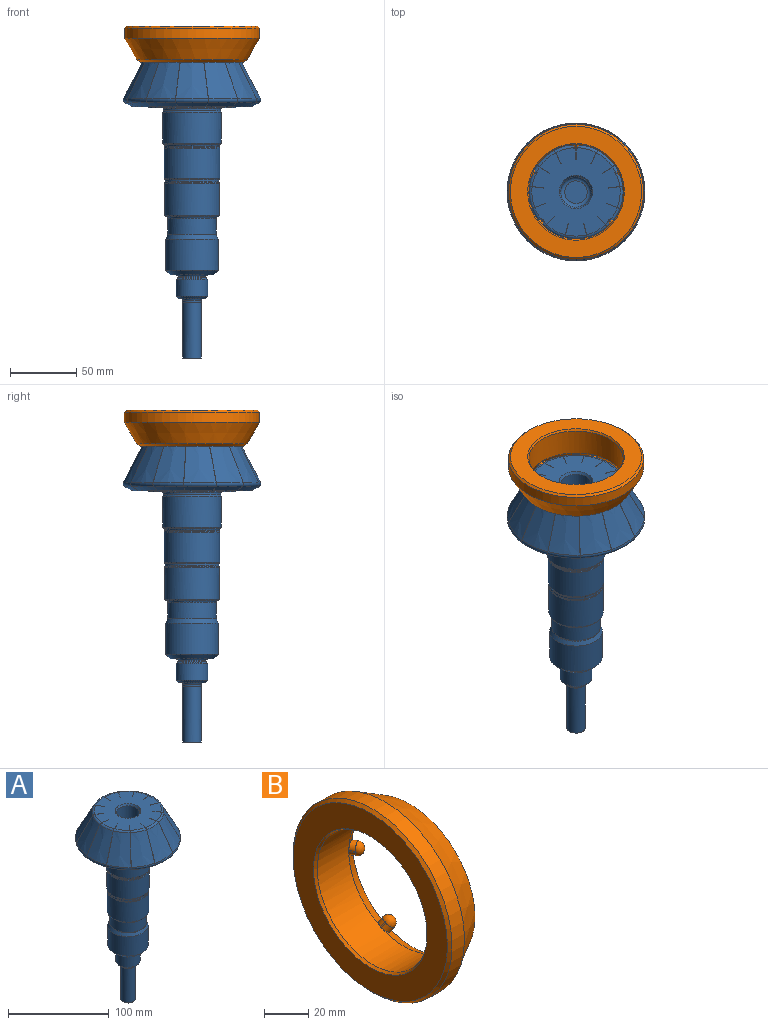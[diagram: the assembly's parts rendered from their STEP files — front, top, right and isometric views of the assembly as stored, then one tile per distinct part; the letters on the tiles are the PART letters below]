
ASSEMBLY  parts=2 mates=1
PART A: 145 faces, bbox 111.8x111x228.1 mm
  f0: cone r=0mm half-angle=45deg, axis (0,0,-1), area 6.9mm2, adj f1
  f1: cylinder r=1.25mm len=2.5mm, axis (0,0,-1), area 7.3mm2, adj f0,f2
  f2: cone r=0mm half-angle=30deg, axis (0,0,-1), area 34.3mm2, adj f1,f3
  f3: cone r=0mm half-angle=60deg, axis (0,0,-1), area 33.6mm2, adj f2,f4
  f4: plane 14x14mm, normal (0,0,-1), area 102.8mm2, adj f3,f5
  f5: cylinder r=7mm len=41.51mm, axis (0,0,1), area 1825.8mm2, adj f4,f6
  f6: cone r=0mm half-angle=20deg, axis (0,0,-1), area 6.4mm2, adj f5,f7
  f7: cylinder r=6.95mm len=13.9mm, axis (0,0,1), area 87.3mm2, adj f6,f8
  f8: torus R=7.95mm, axis (0,0,1), area 72.2mm2, adj f7,f9
  f9: plane 20x20mm, normal (0,0,-1), area 115.6mm2, adj f8,f10
  f10: cone r=0mm half-angle=45deg, axis (0,0,1), area 195.5mm2, adj f9,f11
  f11: cylinder r=12mm len=24mm, axis (0,0,1), area 953.1mm2, adj f10,f12
  f12: cone r=0mm half-angle=50deg, axis (0,0,-1), area 100.7mm2, adj f11,f13
  f13: torus R=11.7mm, axis (0,0,1), area 70.1mm2, adj f12,f14
  f14: cylinder r=10.5mm len=21mm, axis (0,0,1), area 22.5mm2, adj f13,f15
  f15: torus R=11.7mm, axis (0,0,1), area 129.5mm2, adj f14,f16
  f16: plane 33x33mm, normal (0,0,-1), area 425.2mm2, adj f15,f17
  f17: cone r=0mm half-angle=45deg, axis (0,0,1), area 545.4mm2, adj f16,f18
  f18: cylinder r=19.88mm len=39.75mm, axis (0,0,1), area 2938.8mm2, adj f17,f19
  f19: cone r=0mm half-angle=25deg, axis (0,0,-1), area 443.6mm2, adj f18,f20
  f20: torus R=19.4mm, axis (0,0,1), area 60mm2, adj f19,f21
  f21: cylinder r=18.2mm len=36.4mm, axis (0,0,1), area 1376.1mm2, adj f20,f22
  f22: torus R=19.4mm, axis (0,0,1), area 220.7mm2, adj f21,f23
  f23: plane 40.12x40.12mm, normal (0,0,-1), area 81.8mm2, adj f22,f24
  f24: cone r=0mm half-angle=30deg, axis (0,0,1), area 147.6mm2, adj f23,f25
  f25: cylinder r=20.64mm len=41.28mm, axis (0,0,1), area 3145.3mm2, adj f24,f26
  f26: cone r=0mm half-angle=25deg, axis (0,0,-1), area 57.3mm2, adj f25,f27
  f27: torus R=21.54mm, axis (0,0,1), area 67mm2, adj f26,f28
  f28: cylinder r=20.34mm len=40.68mm, axis (0,0,1), area 193.3mm2, adj f27,f29
  f29: torus R=21.54mm, axis (0,0,1), area 80.5mm2, adj f28,f30
  f30: cone r=0mm half-angle=30deg, axis (0,0,1), area 130.8mm2, adj f29,f31
  f31: cylinder r=21mm len=42mm, axis (0,0,1), area 2983.2mm2, adj f30,f32
  f32: cone r=0mm half-angle=25deg, axis (0,0,-1), area 58.3mm2, adj f31,f33
  f33: torus R=21.9mm, axis (0,0,1), area 68.2mm2, adj f32,f34
  f34: cylinder r=20.7mm len=41.4mm, axis (0,0,1), area 82.5mm2, adj f33,f35
  f35: torus R=21.9mm, axis (0,0,1), area 113.4mm2, adj f34,f36
  f36: cylinder r=21mm len=42mm, axis (0,0,1), area 53.6mm2, adj f35,f37
  f37: plane 43.3x43.3mm, normal (0,0,-1), area 86.8mm2, adj f36,f38
  f38: cone r=0mm half-angle=30deg, axis (0,0,1), area 159.2mm2, adj f37,f39
  f39: cylinder r=22.23mm len=44.45mm, axis (0,0,1), area 3259.8mm2, adj f38,f40
  f40: cone r=0mm half-angle=25deg, axis (0,0,-1), area 159.3mm2, adj f39,f41
  f41: torus R=22.46mm, axis (0,0,1), area 47.6mm2, adj f40,f42
  f42: cylinder r=21.66mm len=43.33mm, axis (0,0,1), area 152.8mm2, adj f41,f43
  f43: torus R=22.46mm, axis (0,0,1), area 173.3mm2, adj f42,f45
  f44: plane 17.03x17.01mm, normal (0,0,1), area 227mm2, adj f46
  f45: plane 53.33x53.33mm, normal (0,0,-1), area 648.2mm2, adj f43,f47
  f46: torus R=8.5mm, axis (0,0,-1), area 308.2mm2, adj f44,f48
  f47: cylinder r=26.66mm len=53.33mm, axis (0,0,1), area 25.1mm2, adj f45,f73
  f48: cylinder r=11.5mm len=100mm, axis (0,0,-1), area 7225.7mm2, adj f46,f86
  f49: torus R=49.52mm, axis (0,0,-1), area 97.6mm2, adj f50,f89,f90,f91
  f50: cone r=0mm half-angle=27.8deg, axis (0,0,-1), area 728.3mm2, adj f49,f75,f89,f91
  f51: torus R=49.52mm, axis (0,0,-1), area 97.6mm2, adj f52,f93,f94,f95
  f52: cone r=0mm half-angle=27.8deg, axis (0,0,-1), area 728.3mm2, adj f51,f76,f93,f95
  f53: torus R=49.52mm, axis (0,0,-1), area 97.6mm2, adj f54,f97,f98,f99
  f54: cone r=0mm half-angle=27.8deg, axis (0,0,-1), area 728.3mm2, adj f53,f77,f97,f99
  f55: torus R=49.52mm, axis (0,0,-1), area 97.6mm2, adj f56,f101,f102,f103
  f56: cone r=0mm half-angle=27.8deg, axis (0,0,-1), area 728.3mm2, adj f55,f78,f101,f103
  f57: torus R=49.52mm, axis (0,0,-1), area 97.6mm2, adj f58,f105,f106,f107
  f58: cone r=0mm half-angle=27.8deg, axis (0,0,-1), area 728.3mm2, adj f57,f79,f105,f107
  f59: torus R=49.52mm, axis (0,0,-1), area 97.6mm2, adj f60,f109,f110,f111
  f60: cone r=0mm half-angle=27.8deg, axis (0,0,-1), area 728.3mm2, adj f59,f80,f109,f111
  f61: torus R=49.52mm, axis (0,0,-1), area 97.6mm2, adj f62,f113,f114,f115
  f62: cone r=0mm half-angle=27.8deg, axis (0,0,-1), area 728.3mm2, adj f61,f81,f113,f115
  f63: torus R=49.52mm, axis (0,0,-1), area 97.6mm2, adj f64,f117,f118,f119
  f64: cone r=0mm half-angle=27.8deg, axis (0,0,-1), area 728.3mm2, adj f63,f82,f117,f119
  f65: torus R=49.52mm, axis (0,0,-1), area 97.6mm2, adj f66,f121,f122,f123
  f66: cone r=0mm half-angle=27.8deg, axis (0,0,-1), area 728.3mm2, adj f65,f83,f121,f123
  f67: torus R=49.52mm, axis (0,0,-1), area 97.6mm2, adj f68,f125,f126,f127
  f68: cone r=0mm half-angle=27.8deg, axis (0,0,-1), area 728.3mm2, adj f67,f84,f125,f127
  f69: torus R=49.52mm, axis (0,0,-1), area 97.6mm2, adj f70,f129,f130,f131
  f70: cone r=0mm half-angle=27.8deg, axis (0,0,-1), area 728.3mm2, adj f69,f85,f129,f131
  f71: torus R=49.52mm, axis (0,0,-1), area 97.6mm2, adj f72,f87,f88,f133
  f72: cone r=0mm half-angle=27.8deg, axis (0,0,-1), area 728.3mm2, adj f71,f74,f88,f133
  f73: plane 66x66mm, normal (0,0,-1), area 1187.9mm2, adj f47,f134
  f74: torus R=33.34mm, axis (0,0,-1), area 45.1mm2, adj f72,f88,f133,f138
  f75: torus R=33.34mm, axis (0,0,-1), area 45.1mm2, adj f50,f89,f91,f138
  f76: torus R=33.34mm, axis (0,0,-1), area 45.1mm2, adj f52,f93,f95,f138
  f77: torus R=33.34mm, axis (0,0,-1), area 45.1mm2, adj f54,f97,f99,f138
  f78: torus R=33.34mm, axis (0,0,-1), area 45.1mm2, adj f56,f101,f103,f138
  f79: torus R=33.34mm, axis (0,0,-1), area 45.1mm2, adj f58,f105,f107,f138
  f80: torus R=33.34mm, axis (0,0,-1), area 45.1mm2, adj f60,f109,f111,f138
  f81: torus R=33.34mm, axis (0,0,-1), area 45.1mm2, adj f62,f113,f115,f138
  f82: torus R=33.34mm, axis (0,0,-1), area 45.1mm2, adj f64,f117,f119,f138
  f83: torus R=33.34mm, axis (0,0,-1), area 45.1mm2, adj f66,f121,f123,f138
  f84: torus R=33.34mm, axis (0,0,-1), area 45.1mm2, adj f68,f125,f127,f138
  f85: torus R=33.34mm, axis (0,0,-1), area 45.1mm2, adj f70,f129,f131,f138
  f86: cone r=0mm half-angle=30deg, axis (0,0,1), area 175.2mm2, adj f48,f138
  f87: cone r=0mm half-angle=62.2deg, axis (0,0,1), area 147.6mm2, adj f71,f88,f133,f140
  f88: plane 38.41x27.58mm, normal (1,0,0), area 377.1mm2, adj f71,f72,f74,f87,f135,f138,f140
  f89: plane 38.41x24.42mm, normal (-0.89,0.46,0), area 377.1mm2, adj f49,f50,f75,f90,f138,f139,f140
  f90: cone r=0mm half-angle=62.2deg, axis (0,0,1), area 147.6mm2, adj f49,f89,f91,f140
  f91: plane 38.41x22.7mm, normal (0.57,-0.82,0), area 377.1mm2, adj f49,f50,f75,f90,f92,f138,f140
  f92: plane 38.4x16.7mm, normal (0.73,0.5,0.47), area 4.3mm2, adj f91,f93,f138,f140
  f93: plane 38.41x22.7mm, normal (-0.57,0.82,0), area 377.1mm2, adj f51,f52,f76,f92,f94,f138,f140
  f94: cone r=0mm half-angle=62.2deg, axis (0,0,1), area 147.6mm2, adj f51,f93,f95,f140
  f95: plane 38.41x27.38mm, normal (0.12,-0.99,0), area 377.1mm2, adj f51,f52,f76,f94,f96,f138,f140
  f96: plane 38.4x20.09mm, normal (0.88,0.11,0.47), area 4.3mm2, adj f95,f97,f138,f140
  f97: plane 38.41x27.38mm, normal (-0.12,0.99,0), area 377.1mm2, adj f53,f54,f77,f96,f98,f138,f140
  f98: cone r=0mm half-angle=62.2deg, axis (0,0,1), area 147.6mm2, adj f53,f97,f99,f140
  f99: plane 38.41x25.79mm, normal (-0.35,-0.94,0), area 377.1mm2, adj f53,f54,f77,f98,f100,f138,f140
  f100: plane 38.4x18.95mm, normal (0.83,-0.31,0.47), area 4.3mm2, adj f99,f101,f138,f140
  f101: plane 38.41x25.79mm, normal (0.35,0.94,0), area 377.1mm2, adj f55,f56,f78,f100,f102,f138,f140
  f102: cone r=0mm half-angle=62.2deg, axis (0,0,1), area 147.6mm2, adj f55,f101,f103,f140
  f103: plane 38.41x20.64mm, normal (-0.75,-0.66,0), area 377.1mm2, adj f55,f56,f78,f102,f104,f138,f140
  f104: plane 38.4x15.21mm, normal (0.59,-0.66,0.47), area 4.3mm2, adj f103,f105,f138,f140
  f105: plane 38.41x20.65mm, normal (0.75,0.66,0), area 377.1mm2, adj f57,f58,f79,f104,f106,f138,f140
  f106: cone r=0mm half-angle=62.2deg, axis (0,0,1), area 147.6mm2, adj f57,f105,f107,f140
  f107: plane 38.41x26.78mm, normal (-0.97,-0.24,0), area 377.1mm2, adj f57,f58,f79,f106,f108,f138,f140
  f108: plane 38.4x19.66mm, normal (0.21,-0.86,0.47), area 4.3mm2, adj f107,f109,f138,f140
  f109: plane 38.41x26.78mm, normal (0.97,0.24,0), area 377.1mm2, adj f59,f60,f80,f108,f110,f138,f140
  f110: cone r=0mm half-angle=62.2deg, axis (0,0,1), area 147.6mm2, adj f59,f109,f111,f140
  f111: plane 38.41x26.78mm, normal (-0.97,0.24,0), area 377.1mm2, adj f59,f60,f80,f110,f112,f138,f140
  f112: plane 38.4x19.66mm, normal (-0.21,-0.86,0.47), area 4.3mm2, adj f111,f113,f138,f140
  f113: plane 38.41x26.78mm, normal (0.97,-0.24,0), area 377.1mm2, adj f61,f62,f81,f112,f114,f138,f140
  f114: cone r=0mm half-angle=62.2deg, axis (0,0,1), area 147.6mm2, adj f61,f113,f115,f140
  f115: plane 38.41x20.64mm, normal (-0.75,0.66,0), area 377.1mm2, adj f61,f62,f81,f114,f116,f138,f140
  f116: plane 38.4x15.21mm, normal (-0.59,-0.66,0.47), area 4.3mm2, adj f115,f117,f138,f140
  f117: plane 38.41x20.65mm, normal (0.75,-0.66,0), area 377.1mm2, adj f63,f64,f82,f116,f118,f138,f140
  f118: cone r=0mm half-angle=62.2deg, axis (0,0,1), area 147.6mm2, adj f63,f117,f119,f140
  f119: plane 38.41x25.79mm, normal (-0.35,0.94,0), area 377.1mm2, adj f63,f64,f82,f118,f120,f138,f140
  f120: plane 38.4x18.95mm, normal (-0.83,-0.31,0.47), area 4.3mm2, adj f119,f121,f138,f140
  f121: plane 38.41x25.79mm, normal (0.35,-0.94,0), area 377.1mm2, adj f65,f66,f83,f120,f122,f138,f140
  f122: cone r=0mm half-angle=62.2deg, axis (0,0,1), area 147.6mm2, adj f65,f121,f123,f140
  f123: plane 38.41x27.38mm, normal (0.12,0.99,0), area 377.1mm2, adj f65,f66,f83,f122,f124,f138,f140
  f124: plane 38.4x20.09mm, normal (-0.88,0.11,0.47), area 4.3mm2, adj f123,f125,f138,f140
  f125: plane 38.41x27.38mm, normal (-0.12,-0.99,0), area 377.1mm2, adj f67,f68,f84,f124,f126,f138,f140
  f126: cone r=0mm half-angle=62.2deg, axis (0,0,1), area 147.6mm2, adj f67,f125,f127,f140
  f127: plane 38.41x22.7mm, normal (0.57,0.82,0), area 377.1mm2, adj f67,f68,f84,f126,f128,f138,f140
  f128: plane 38.4x16.7mm, normal (-0.73,0.5,0.47), area 4.3mm2, adj f127,f129,f138,f140
  f129: plane 38.41x22.7mm, normal (-0.57,-0.82,0), area 377.1mm2, adj f69,f70,f85,f128,f130,f138,f140
  f130: cone r=0mm half-angle=62.2deg, axis (0,0,1), area 147.6mm2, adj f69,f129,f131,f140
  f131: plane 38.41x24.42mm, normal (0.89,0.46,0), area 377.1mm2, adj f69,f70,f85,f130,f132,f138,f140
  f132: plane 38.4x17.96mm, normal (-0.41,0.78,0.47), area 4.3mm2, adj f131,f133,f138,f140
  f133: plane 38.41x24.42mm, normal (-0.89,-0.46,0), area 377.1mm2, adj f71,f72,f74,f87,f132,f138,f140
  f134: cylinder r=33mm len=66mm, axis (0,0,-1), area 207.3mm2, adj f73,f140
  f135: plane 38.4x20.23mm, normal (0,0.88,0.47), area 4.3mm2, adj f88,f138,f140,f141
  f136: cone r=0mm half-angle=27.8deg, axis (0,0,-1), area 728.3mm2, adj f137,f141,f142,f143
  f137: torus R=33.34mm, axis (0,0,-1), area 45.1mm2, adj f136,f138,f141,f143
  f138: plane 66.69x66.69mm, normal (0,0,1), area 2978.4mm2, adj f74,f75,f76,f77,f78,f79,f80,f81
  f139: plane 38.4x17.96mm, normal (0.41,0.78,0.47), area 4.3mm2, adj f89,f138,f140,f143
  f140: plane 90.02x90.02mm, normal (0,0,-1), area 2942.8mm2, adj f87,f88,f89,f90,f91,f92,f93,f94
  f141: plane 38.4x27.58mm, normal (-1,0,0), area 377.1mm2, adj f135,f136,f137,f138,f140,f142,f144
  f142: torus R=49.52mm, axis (0,0,-1), area 97.6mm2, adj f136,f141,f143,f144
  f143: plane 38.41x24.42mm, normal (0.89,-0.46,0), area 377.1mm2, adj f136,f137,f138,f139,f140,f142,f144
  f144: cone r=0mm half-angle=62.2deg, axis (0,0,1), area 147.6mm2, adj f140,f141,f142,f143
PART B: 37 faces, bbox 30.8x103.3x103.3 mm
  f0: plane 4.35x3.07mm, normal (-0.87,-0.5,0), area 2.2mm2, adj f1,f20,f21,f23
  f1: cylinder r=35.56mm len=71.12mm, axis (-1,0,0), area 4512.5mm2, adj f0,f2,f3,f4,f5,f6,f7,f10
  f2: cone r=36mm half-angle=30deg, axis (-1,0,0), area 398mm2, adj f1,f26
  f3: cone r=37.13mm half-angle=30deg, axis (1,0,0), area 232.4mm2, adj f1,f8,f23,f27
  f4: cone r=37.13mm half-angle=30deg, axis (1,0,0), area 228.3mm2, adj f1,f8,f29,f32
  f5: cone r=37.13mm half-angle=30deg, axis (1,0,0), area 366.1mm2, adj f1,f8,f10,f34
  f6: cone r=37.13mm half-angle=30deg, axis (1,0,0), area 228.4mm2, adj f1,f8,f17,f20
  f7: cone r=37.13mm half-angle=30deg, axis (1,0,0), area 228.4mm2, adj f1,f8,f12,f15
  f8: cone r=40.22mm half-angle=60deg, axis (-1,0,0), area 886.8mm2, adj f3,f4,f5,f6,f7,f9,f10,f12
  f9: cone r=46.36mm half-angle=30deg, axis (-1,0,0), area 5381mm2, adj f8,f24
  f10: cylinder r=3.17mm len=7.08mm, axis (-0.5,-0.56,-0.66), area 30.5mm2, adj f1,f5,f8,f11,f13,f14
  f11: plane 3.93x3.66mm, normal (-0.87,0.32,0.38), area 2.2mm2, adj f1,f10,f12,f14
  f12: cylinder r=3.17mm len=7.08mm, axis (0.5,0.56,0.66), area 30.5mm2, adj f1,f7,f8,f11,f13,f14
  f13: plane 3.9x3.63mm, normal (0.87,-0.32,-0.38), area 2.2mm2, adj f8,f10,f12,f14
  f14: torus R=0.33mm, axis (-0.87,0.32,0.38), area 180.8mm2, adj f10,f11,f12,f13
  f15: cylinder r=3.17mm len=7.08mm, axis (-0.5,0.36,-0.79), area 30.5mm2, adj f1,f7,f8,f16,f18,f19
  f16: plane 4.24x3.08mm, normal (-0.87,-0.21,0.45), area 2.2mm2, adj f1,f15,f17,f19
  f17: cylinder r=3.17mm len=7.08mm, axis (0.5,-0.36,0.79), area 30.5mm2, adj f1,f6,f8,f16,f18,f19
  f18: plane 4.21x3.07mm, normal (0.87,0.21,-0.45), area 2.2mm2, adj f8,f15,f17,f19
  f19: torus R=0.33mm, axis (-0.87,-0.21,0.45), area 180.8mm2, adj f15,f16,f17,f18
  f20: cylinder r=3.17mm len=7.08mm, axis (-0.5,0.87,-0.01), area 30.5mm2, adj f0,f1,f6,f8,f21,f22
  f21: torus R=0.33mm, axis (-0.87,-0.5,0), area 180.8mm2, adj f0,f20,f22,f23
  f22: plane 4.32x3.05mm, normal (0.87,0.5,0), area 2.2mm2, adj f8,f20,f21,f23
  f23: cylinder r=3.17mm len=7.08mm, axis (0.5,-0.87,0.01), area 30.5mm2, adj f0,f1,f3,f8,f21,f22
  f24: cylinder r=50.98mm len=101.96mm, axis (-1,0,0), area 2527.8mm2, adj f9,f25
  f25: cone r=50.22mm half-angle=45deg, axis (1,0,0), area 680mm2, adj f24,f26
  f26: plane 98.91x98.91mm, normal (-1,0,0), area 3511.7mm2, adj f2,f25
  f27: cylinder r=3.17mm len=7.08mm, axis (-0.5,0.36,0.79), area 30.5mm2, adj f1,f3,f8,f28,f30,f31
  f28: plane 3.01x1.83mm, normal (-0.87,-0.21,-0.46), area 2.2mm2, adj f1,f27,f29,f31
  f29: cylinder r=3.17mm len=7.08mm, axis (0.5,-0.36,-0.79), area 30.5mm2, adj f1,f4,f8,f28,f30,f31
  f30: plane 2.98x1.82mm, normal (0.87,0.21,0.46), area 2.2mm2, adj f8,f27,f29,f31
  f31: torus R=0.33mm, axis (-0.87,-0.21,-0.46), area 73.7mm2, adj f27,f28,f29,f30
  f32: cylinder r=3.17mm len=7.08mm, axis (-0.5,-0.56,0.66), area 30.5mm2, adj f1,f4,f8,f33,f35,f36
  f33: plane 2.68x2.43mm, normal (-0.87,0.33,-0.38), area 2.2mm2, adj f1,f32,f34,f36
  f34: cylinder r=3.17mm len=7.08mm, axis (0.5,0.56,-0.66), area 30.5mm2, adj f1,f5,f8,f33,f35,f36
  f35: plane 2.65x2.4mm, normal (0.87,-0.33,0.38), area 2.2mm2, adj f8,f32,f34,f36
  f36: torus R=0.33mm, axis (-0.87,0.33,-0.38), area 73.7mm2, adj f32,f33,f34,f35
PLACE A at identity
PLACE B rot(axis=(0,1,0),90deg) t=(0,0,-4.7)mm
MATE revolute B.f1 <-> A.f0  axis (0,0,1) through (0,0,-71.01)mm
